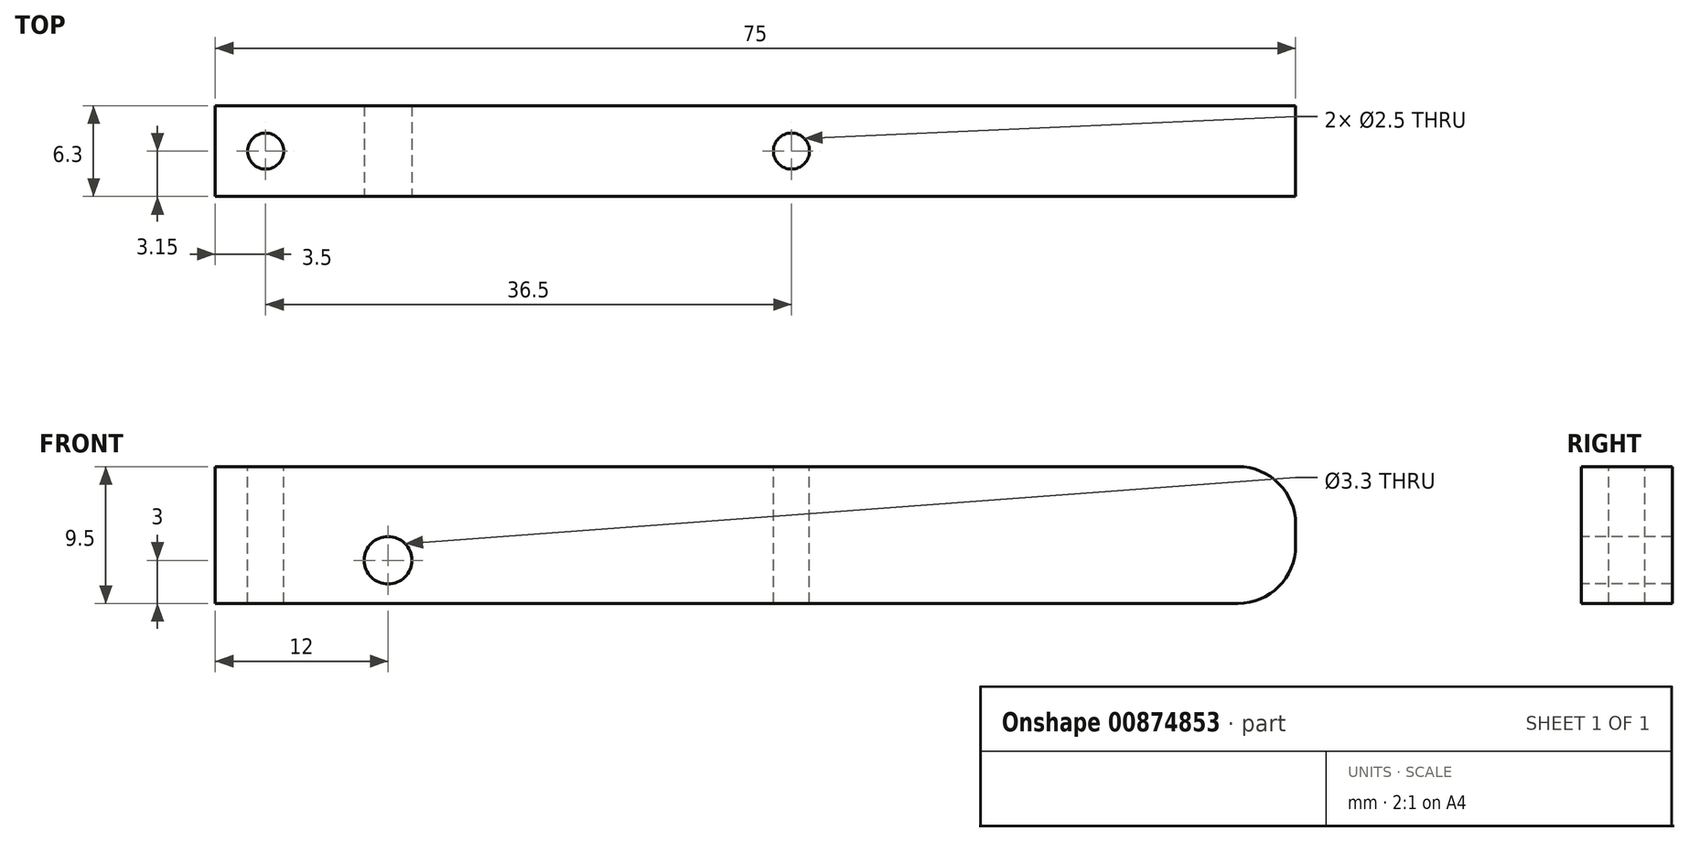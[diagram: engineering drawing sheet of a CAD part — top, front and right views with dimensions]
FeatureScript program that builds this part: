
annotation { "Feature Type Name" : "Feature", "Feature Type Description" : "" }
export const myFeature = defineFeature(function(context is Context, id is Id, definition is map)
    precondition{}
    {
        {
            var Q0;
            Q0=qCreatedBy(makeId("Front.planeOp"),FACE);
            var sketch = newSketch(context, id + "F0", { "sketchPlane" : qUnion([Q0])});
            skLineSegment(sketch, "E0.bottom", {"start": v(0, 0) * mm, "end": v(75, 0) * mm});
            skLineSegment(sketch, "E0.top", {"start": v(0, 9.5) * mm, "end": v(75, 9.5) * mm});
            skLineSegment(sketch, "E0.left", {"start": v(0, 0) * mm, "end": v(0, 9.5) * mm});
            skLineSegment(sketch, "E0.right", {"start": v(75, 0) * mm, "end": v(75, 9.5) * mm});
            skSolve(sketch);
        }
        {
            var Q0;
            Q0 = qSketchRegion(id + "F0", true);
            extrude(context, id + "F1", {"entities" : qUnion([Q0]), "depth" : 6.3 * mm, "offsetDistance" : 25 * mm});
        }
        {
            var Q0;
            Q0=makeQuery(id+"F1.opExtrude","SWEPT_FACE",FACE,{"disambiguationData":[OSD([sQuery(id+"F0.wireOp",EDGE,"E0.top")])]});
            var sketch = newSketch(context, id + "F2", { "sketchPlane" : qUnion([Q0])});
            skPoint(sketch, "E1", {"position": v(3.5, -3.15) * mm});
            skPoint(sketch, "E1.positionSnap0", {"position": v(0, -3.15) * mm});
            skPoint(sketch, "E2", {"position": v(40, -3.15) * mm});
            skSolve(sketch);
        }
        {
            var Q0;
            Q0=sQuery(id+"F2.wireOp",VERTEX,"E1");
            var Q1;
            Q1=sQuery(id+"F2.wireOp",VERTEX,"E2");
            var Q2;
            Q2=makeQuery(id+"F1.opExtrude","SWEPT_BODY",BODY,{"disambiguationData":[OSD([sQuery(id+"F0.wireOp",EDGE,"E0.bottom"),sQuery(id+"F0.wireOp",EDGE,"E0.top"),sQuery(id+"F0.wireOp",EDGE,"E0.left"),sQuery(id+"F0.wireOp",EDGE,"E0.right")])]});
            hole(context, id + "F3", {"style" : HoleStyle.SIMPLE, "endStyle" : HoleEndStyle.THROUGH, "standardTappedOrClearance" : lookupTablePath({ "standard" : "ISO", "engagement" : "75%", "pitch" : "0.5 mm", "size" : "M3", "type" : "Tapped" }), "standardBlindInLast" : lookupTablePath({ "standard" : "ISO", "engagement" : "75%", "pitch" : "0.5 mm", "size" : "M3", "type" : "Tapped" }), "holeDiameter" : 2.5 * mm, "majorDiameter" : 3 * mm, "showTappedDepth" : true, "isTappedThrough" : true, "tappedDepth" : 11.5 * mm, "tapClearance" : 3, "locations" : qUnion([Q0, Q1]), "scope" : qUnion([Q2])});
        }
        {
            var Q0;
            Q0=makeQuery(id+"F1.opExtrude","CAP_FACE",FACE,{"disambiguationData":[OSD([sQuery(id+"F0.wireOp",EDGE,"E0.bottom"),sQuery(id+"F0.wireOp",EDGE,"E0.top"),sQuery(id+"F0.wireOp",EDGE,"E0.left"),sQuery(id+"F0.wireOp",EDGE,"E0.right")])],"isStart":false});
            var sketch = newSketch(context, id + "F4", { "sketchPlane" : qUnion([Q0])});
            skPoint(sketch, "E3", {"position": v(12, 3) * mm});
            skSolve(sketch);
        }
        {
            var Q0;
            Q0=sQuery(id+"F4.wireOp",VERTEX,"E3");
            var Q1;
            Q1=makeQuery(id+"F1.opExtrude","SWEPT_BODY",BODY,{"disambiguationData":[OSD([sQuery(id+"F0.wireOp",EDGE,"E0.bottom"),sQuery(id+"F0.wireOp",EDGE,"E0.top"),sQuery(id+"F0.wireOp",EDGE,"E0.left"),sQuery(id+"F0.wireOp",EDGE,"E0.right")])]});
            hole(context, id + "F5", {"style" : HoleStyle.SIMPLE, "endStyle" : HoleEndStyle.THROUGH, "standardTappedOrClearance" : lookupTablePath({ "fit" : "Normal", "standard" : "ISO", "size" : "M3", "type" : "Clearance" }), "standardBlindInLast" : lookupTablePath({ "fit" : "Standard", "standard" : "ISO", "size" : "M3", "type" : "Clearance" }), "holeDiameter" : 3.3 * mm, "majorDiameter" : 3 * mm, "isTappedThrough" : true, "tappedDepth" : 11.5 * mm, "tapClearance" : 3, "locations" : qUnion([Q0]), "scope" : qUnion([Q1])});
        }
        {
            var Q0;
            Q0=makeQuery(id+"F1.opExtrude","SWEPT_EDGE",EDGE,{"disambiguationData":[OSD([sQuery(id+"F0.wireOp",EDGE,"E0.top"),sQuery(id+"F0.wireOp",EDGE,"E0.right")])]});
            var Q1;
            Q1=makeQuery(id+"F1.opExtrude","SWEPT_EDGE",EDGE,{"disambiguationData":[OSD([sQuery(id+"F0.wireOp",EDGE,"E0.bottom"),sQuery(id+"F0.wireOp",EDGE,"E0.right")])]});
            fillet(context, id + "F6", {"entities" : qUnion([Q0, Q1]), "radius" : 4 * mm, "tangentPropagation" : true, "allowEdgeOverflow" : false});
        }
    });
